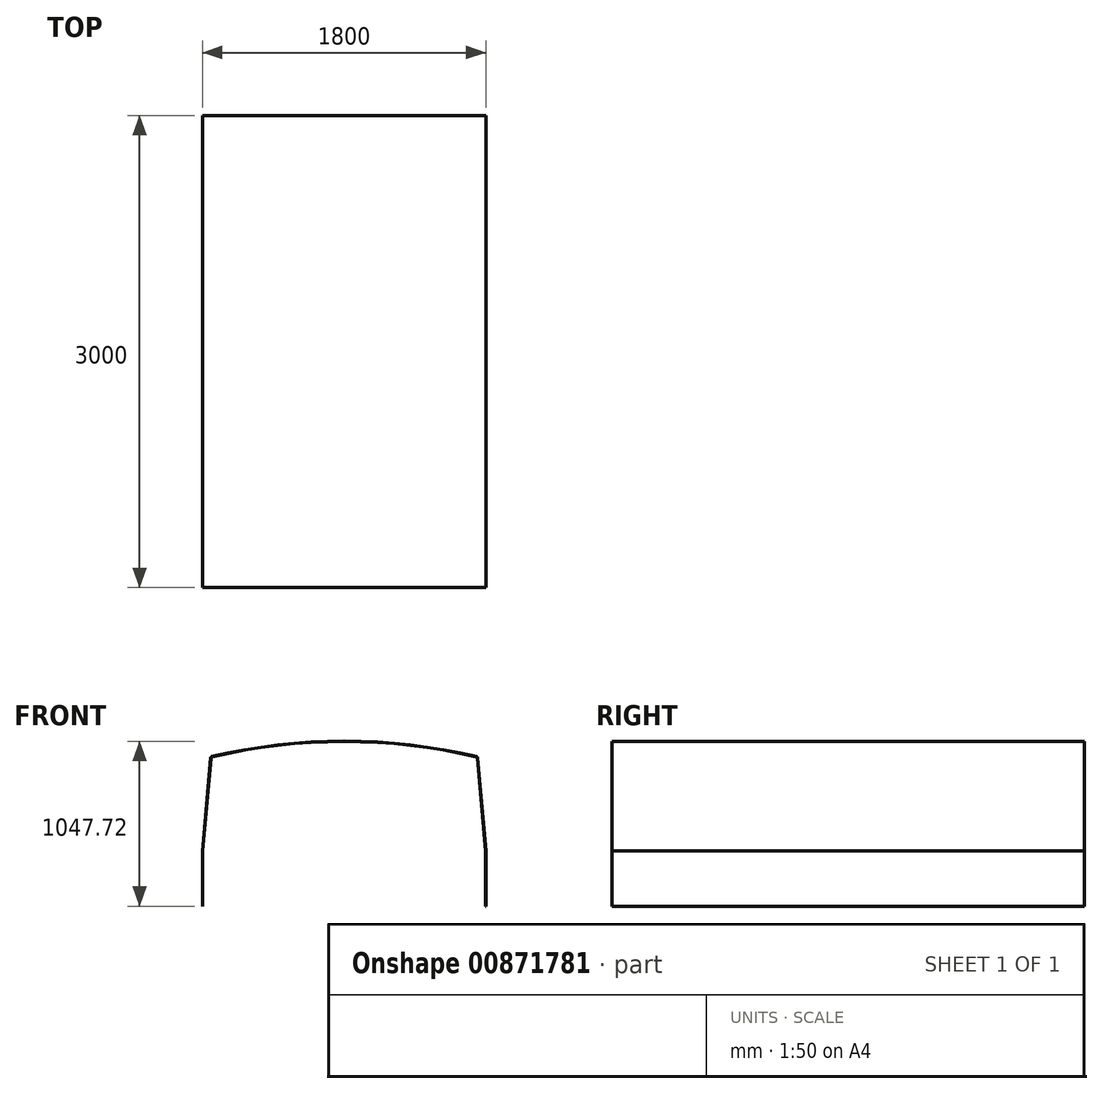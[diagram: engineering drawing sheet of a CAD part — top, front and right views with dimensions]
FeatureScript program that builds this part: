
annotation { "Feature Type Name" : "Feature", "Feature Type Description" : "" }
export const myFeature = defineFeature(function(context is Context, id is Id, definition is map)
    precondition{}
    {
        {
            var Q0;
            Q0=qCreatedBy(makeId("Front.planeOp"),FACE);
            var sketch = newSketch(context, id + "F0", { "sketchPlane" : qUnion([Q0])});
            skLineSegment(sketch, "E0", {"start": v(0, 118.58) * mm, "end": v(0, -81.11) * mm, "construction": true});
            skSolve(sketch);
        }
        {
            var Q0;
            Q0=qCreatedBy(makeId("Front.planeOp"),FACE);
            var sketch = newSketch(context, id + "F1", { "sketchPlane" : qUnion([Q0])});
            skLineSegment(sketch, "E1", {"start": v(-900, 0) * mm, "end": v(-900, 350) * mm});
            skLineSegment(sketch, "E2", {"start": v(-900, 350) * mm, "end": v(-847.7, 947.72) * mm});
            skLineSegment(sketch, "E3", {"start": v(-847.7, 947.72) * mm, "end": v(0, 947.72) * mm, "construction": true});
            skPoint(sketch, "E4", {"position": v(0, 1047.72) * mm});
            skArc(sketch, "E5", {"start": v(-847.7, 947.72) * mm, "mid": v(-426.8, 1022.63) * mm, "end": v(0, 1047.72) * mm});
            skArc(sketch, "E6.MirrorCS", {"start": v(847.7, 947.72) * mm, "mid": v(426.8, 1022.63) * mm, "end": v(0, 1047.72) * mm});
            skLineSegment(sketch, "E7.MirrorCS", {"start": v(900, 0) * mm, "end": v(900, 350) * mm});
            skLineSegment(sketch, "E8.MirrorCS", {"start": v(900, 350) * mm, "end": v(847.7, 947.72) * mm});
            skArc(sketch, "E9.0", {"start": v(-845.84, 946.1) * mm, "mid": v(-425.84, 1020.73) * mm, "end": v(0, 1045.72) * mm});
            skLineSegment(sketch, "E10.0", {"start": v(-898, 349.91) * mm, "end": v(-845.84, 946.1) * mm});
            skLineSegment(sketch, "E11.0", {"start": v(-898, 0) * mm, "end": v(-898, 349.91) * mm});
            skLineSegment(sketch, "E12", {"start": v(-898, 0) * mm, "end": v(-900, 0) * mm});
            skArc(sketch, "E13.MirrorCS", {"start": v(845.84, 946.1) * mm, "mid": v(425.84, 1020.73) * mm, "end": v(0, 1045.72) * mm});
            skLineSegment(sketch, "E14.MirrorCS", {"start": v(898, 349.91) * mm, "end": v(845.84, 946.1) * mm});
            skLineSegment(sketch, "E15.MirrorCS", {"start": v(898, 0) * mm, "end": v(898, 349.91) * mm});
            skLineSegment(sketch, "E16.MirrorCS", {"start": v(898, 0) * mm, "end": v(900, 0) * mm});
            skSolve(sketch);
        }
        {
            var Q0;
            Q0 = qSketchRegion(id + "F1", true);
            extrude(context, id + "F2", {"entities" : qUnion([Q0]), "depth" : 1500 * mm, "offsetDistance" : 25 * mm, "hasSecondDirection" : true, "secondDirectionOppositeDirection" : true, "secondDirectionDepth" : 1500 * mm});
        }
        {
            var Q0;
            Q0=makeQuery(id+"F2.opExtrude","SWEPT_EDGE",EDGE,{"disambiguationData":[OSD([sQuery(id+"F1.wireOp",EDGE,"E9.0"),sQuery(id+"F1.wireOp",EDGE,"E10.0")])]});
            fillet(context, id + "F3", {"entities" : qUnion([Q0]), "radius" : 10 * mm, "tangentPropagation" : true, "allowEdgeOverflow" : false});
        }
        {
            var Q0;
            Q0=makeQuery(id+"F2.opExtrude","SWEPT_EDGE",EDGE,{"disambiguationData":[OSD([sQuery(id+"F1.wireOp",EDGE,"E2"),sQuery(id+"F1.wireOp",EDGE,"E5")])]});
            fillet(context, id + "F4", {"entities" : qUnion([Q0]), "radius" : 10 * mm, "tangentPropagation" : true, "allowEdgeOverflow" : false});
        }
        {
            var Q0;
            Q0=makeQuery(id+"F2.opExtrude","SWEPT_EDGE",EDGE,{"disambiguationData":[OSD([sQuery(id+"F1.wireOp",EDGE,"E6.MirrorCS"),sQuery(id+"F1.wireOp",EDGE,"E8.MirrorCS")])]});
            fillet(context, id + "F5", {"entities" : qUnion([Q0]), "radius" : 10 * mm, "tangentPropagation" : true, "allowEdgeOverflow" : false});
        }
        {
            var Q0;
            Q0=makeQuery(id+"F2.opExtrude","SWEPT_EDGE",EDGE,{"disambiguationData":[OSD([sQuery(id+"F1.wireOp",EDGE,"E13.MirrorCS"),sQuery(id+"F1.wireOp",EDGE,"E14.MirrorCS")])]});
            fillet(context, id + "F6", {"entities" : qUnion([Q0]), "radius" : 10 * mm, "tangentPropagation" : true, "allowEdgeOverflow" : false});
        }
    });
